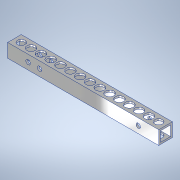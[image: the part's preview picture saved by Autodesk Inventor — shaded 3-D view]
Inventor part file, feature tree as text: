
AUTODESK INVENTOR PART (.ipt)
format: ipt  version: 2020.3 (Build 243373000, 373)  size: 261,632 bytes
history: native  units: mm
features: sketch x6, hole x5, other x1, extrude x1
ambient origin geometry x8: Origin, YZ Plane, XZ Plane, XY Plane, X Axis, Y Axis, Z Axis, Center Point
bodies: Body1 (feature_tree)
feature tree (13):
  other  "ソリッド1"
  extrude  "押し出し1"  Depth=9.0mm
  hole  "穴1"  [1 undecoded]
  hole  "穴2"  [1 undecoded]
  hole  "穴4"  [1 undecoded]
  hole  "穴5"  [1 undecoded]
  hole  "穴6"  [1 undecoded]
  sketch  "スケッチ1"
  sketch  "スケッチ2"
  sketch  "スケッチ3"
  sketch  "スケッチ5"
  sketch  "スケッチ6"
  sketch  "スケッチ7"
note: 5 required parameter values undecoded (feature->parameter linkage not recoverable at this tier; creation-order binding heuristic only, values carry confidence <= 0.55)
